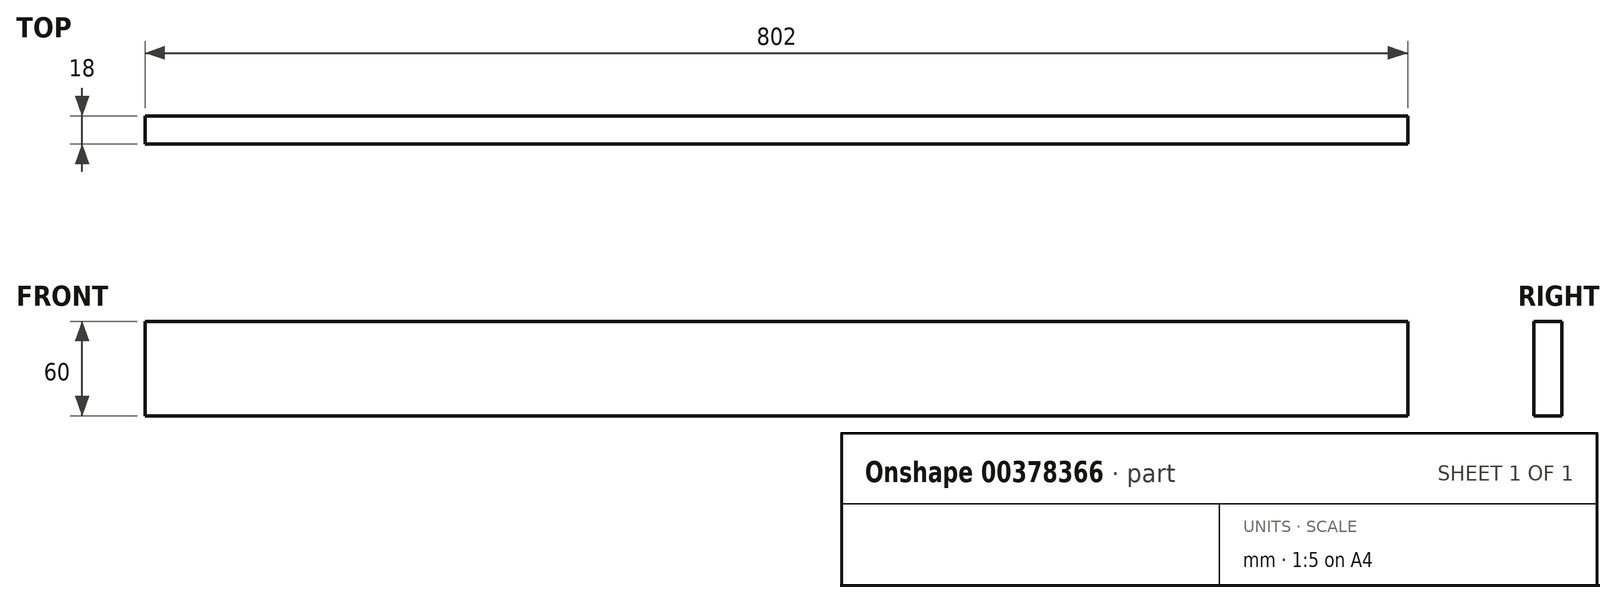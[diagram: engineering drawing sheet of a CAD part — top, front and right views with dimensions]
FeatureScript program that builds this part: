
annotation { "Feature Type Name" : "Feature", "Feature Type Description" : "" }
export const myFeature = defineFeature(function(context is Context, id is Id, definition is map)
    precondition{}
    {
        {
            var Q0;
            Q0=qCreatedBy(makeId("Right.planeOp"),FACE);
            var sketch = newSketch(context, id + "F0", { "sketchPlane" : qUnion([Q0])});
            skLineSegment(sketch, "E0.bottom", {"start": v(9, 30) * mm, "end": v(-9, 30) * mm});
            skLineSegment(sketch, "E0.top", {"start": v(9, -30) * mm, "end": v(-9, -30) * mm});
            skLineSegment(sketch, "E0.left", {"start": v(9, 30) * mm, "end": v(9, -30) * mm});
            skLineSegment(sketch, "E0.right", {"start": v(-9, 30) * mm, "end": v(-9, -30) * mm});
            skPoint(sketch, "E0.middle", {"position": v(0, 0) * mm});
            skSolve(sketch);
        }
        {
            var Q0;
            Q0 = qSketchRegion(id + "F0", true);
            extrude(context, id + "F1", {"entities" : qUnion([Q0]), "depth" : 802 * mm});
        }
    });
